# Revit family: FILTRATION FINALE SIMPLE-DUPLEX
name_source: partatom
category: Equipement de génie climatique
revit_build: Autodesk Revit 2018 (Build: 20170223_1515(x64)
units: mm (PartAtom-declared; Revit-internal decimal feet)

## family parameters
Basée sur le plan de construction = Non
Classification = Aucun
Cote de connecteur circulaire = Utiliser le diamètre
Couper avec des vides une fois chargée = Non
Partagée = Non
Point de calcul de pièce = Non
Toujours verticalement = Oui
Type d'élément = Normal

## types (10) — shared parameters

## per-type parameters (varying)
- FP 036 S: DESCR_ASPI=Entrée filtration; max.36m3/h; G1/2"FEM; DESCR_REFOUL=Sortie filtration; max.36m3/h; G1/2"FEM; DIAM_ASPI_AIR=15 mm  [stored 0.0492126 ft]; DIAM_REFOUL_AIR=15 mm  [stored 0.0492126 ft]; DUPLEX=Non; Debit_aspiration_air=36.0 m³/h; Debit_refoulement_air=36.0 m³/h; HAUTEUR=304 mm; HAUT_VANNE_VERTICALE=42.5 mm; LARGEUR=92 mm  [stored 0.301837 ft]; LARG_FIX=91.6 mm; LONGUEUR=449 mm; OFFEST_FILTRE=100 mm  [stored 0.328084 ft]; OFFEST_TUY1=25 mm  [stored 0.082021 ft]; OFFSET_CLAPET=228 mm; OFFSET_HAUT_TUY=425 mm; OFFSET_TUY2=416 mm; OFFSET_VANNE=25 mm  [stored 0.082021 ft]; OFFSET_VANNE2=345 mm; OFFSET_VANNE_VERTICALE=182 mm; POIDS(Kg)=2.5 mm  [stored 0.0082021 ft]; TAILLE_FILTRE=Filtre_Air_réduit : PAR 036; TAILLE_VANNE=Vanne papillon BS FF : DN15 - G1/2" - FF (231 0002)
- FP 072 S: DESCR_ASPI=Entrée filtration; max.72m3/h; G1/2"FEM; DESCR_REFOUL=Sortie filtration; max.72m3/h; G1/2"FEM; DIAM_ASPI_AIR=15 mm  [stored 0.0492126 ft]; DIAM_REFOUL_AIR=15 mm  [stored 0.0492126 ft]; DUPLEX=Non; Debit_aspiration_air=72.0 m³/h; Debit_refoulement_air=72.0 m³/h; HAUTEUR=352 mm; HAUT_VANNE_VERTICALE=71 mm  [stored 0.23294 ft]; LARGEUR=106 mm  [stored 0.347769 ft]; LARG_FIX=129 mm  [stored 0.423228 ft]; LONGUEUR=471 mm; OFFEST_FILTRE=111 mm; OFFEST_TUY1=99.9 mm; OFFSET_CLAPET=250 mm; OFFSET_HAUT_TUY=425 mm; OFFSET_TUY2=438 mm; OFFSET_VANNE=25 mm  [stored 0.082021 ft]; OFFSET_VANNE2=367 mm; OFFSET_VANNE_VERTICALE=205 mm; POIDS(Kg)=3 mm  [stored 0.00984252 ft]; TAILLE_FILTRE=Filtre_Air_réduit : PAR 072; TAILLE_VANNE=Vanne papillon BS FF : DN15 - G1/2" - FF (231 0002)
- FP 109 S: DESCR_ASPI=Entrée filtration; max.109m3/h; G3/4"FEM; DESCR_REFOUL=Sortie filtration; max.109m3/h; G3/4"FEM; DIAM_ASPI_AIR=20 mm  [stored 0.0656168 ft]; DIAM_REFOUL_AIR=20 mm  [stored 0.0656168 ft]; DUPLEX=Non; Debit_aspiration_air=109.0 m³/h; Debit_refoulement_air=109.0 m³/h; HAUTEUR=361 mm; HAUT_VANNE_VERTICALE=83 mm  [stored 0.27231 ft]; LARGEUR=106 mm  [stored 0.347769 ft]; LARG_FIX=129 mm  [stored 0.423228 ft]; LONGUEUR=508 mm; OFFEST_FILTRE=120 mm  [stored 0.393701 ft]; OFFEST_TUY1=99.9 mm; OFFSET_CLAPET=270 mm; OFFSET_HAUT_TUY=425 mm; OFFSET_TUY2=472 mm; OFFSET_VANNE=27 mm  [stored 0.0885827 ft]; OFFSET_VANNE2=391 mm; OFFSET_VANNE_VERTICALE=220 mm; POIDS(Kg)=4 mm  [stored 0.0131234 ft]; TAILLE_FILTRE=Filtre_Air_réduit : PAR 109; TAILLE_VANNE=Vanne papillon BS FF : DN20 - G3/4" - FF (231 0008)
- FP 396 S: DESCR_ASPI=Entrée filtration; max.396m3/h; G1"FEM; DESCR_REFOUL=Sortie filtration; max.396m3/h; G1"FEM; DIAM_ASPI_AIR=25 mm  [stored 0.082021 ft]; DIAM_REFOUL_AIR=25 mm  [stored 0.082021 ft]; DUPLEX=Non; Debit_aspiration_air=396.0 m³/h; Debit_refoulement_air=396.0 m³/h; HAUTEUR=496 mm; HAUT_VANNE_VERTICALE=93.5 mm  [stored 0.306759 ft]; LARGEUR=131 mm  [stored 0.42979 ft]; LARG_FIX=161 mm; LONGUEUR=620 mm; OFFEST_FILTRE=155 mm  [stored 0.50853 ft]; OFFEST_TUY1=99.9 mm; OFFSET_CLAPET=341 mm; OFFSET_HAUT_TUY=425 mm; OFFSET_TUY2=575 mm; OFFSET_VANNE=34.5 mm  [stored 0.113189 ft]; OFFSET_VANNE2=482 mm; OFFSET_VANNE_VERTICALE=284 mm; POIDS(Kg)=6.5 mm  [stored 0.0213255 ft]; TAILLE_FILTRE=Filtre_Air_réduit : PAR 396; TAILLE_VANNE=Vanne papillon BS FF : DN25 - G1" - FF (231 0001)
- FP 072 DP: DESCR_ASPI=Entrée filtration; max.72m3/h; G1/2"FEM; DESCR_REFOUL=Sortie filtration; max.72m3/h; G1/2"FEM; DIAM_ASPI_AIR=15 mm  [stored 0.0492126 ft]; DIAM_REFOUL_AIR=15 mm  [stored 0.0492126 ft]; DUPLEX=Oui; Debit_aspiration_air=72.0 m³/h; Debit_refoulement_air=72.0 m³/h; HAUTEUR=610 mm; HAUT_VANNE_VERTICALE=71 mm  [stored 0.23294 ft]; LARGEUR=92 mm  [stored 0.301837 ft]; LARG_FIX=108 mm  [stored 0.354331 ft]; LONGUEUR=529 mm; OFFEST_FILTRE=177 mm; OFFEST_TUY1=34 mm; OFFSET_CLAPET=306 mm; OFFSET_HAUT_TUY=306 mm; OFFSET_TUY2=494 mm; OFFSET_VANNE=104 mm; OFFSET_VANNE2=423 mm; OFFSET_VANNE_VERTICALE=260 mm; POIDS(Kg)=5.5 mm  [stored 0.0180446 ft]; TAILLE_FILTRE=Filtre_Air_réduit : PAR 036; TAILLE_VANNE=Vanne papillon BS FF : DN15 - G1/2" - FF (231 0002)
- FP 217 S: DESCR_ASPI=Entrée filtration; max.217m3/h; G3/4"FEM; DESCR_REFOUL=Sortie filtration; max.217m3/h; G3/4"FEM; DIAM_ASPI_AIR=20 mm  [stored 0.0656168 ft]; DIAM_REFOUL_AIR=20 mm  [stored 0.0656168 ft]; DUPLEX=Non; Debit_aspiration_air=217.0 m³/h; Debit_refoulement_air=217.0 m³/h; HAUTEUR=388 mm; HAUT_VANNE_VERTICALE=83 mm  [stored 0.27231 ft]; LARGEUR=131 mm  [stored 0.42979 ft]; LARG_FIX=161 mm; LONGUEUR=541 mm; OFFEST_FILTRE=137 mm  [stored 0.449475 ft]; OFFEST_TUY1=99.9 mm; OFFSET_CLAPET=303 mm; OFFSET_HAUT_TUY=425 mm; OFFSET_TUY2=504 mm; OFFSET_VANNE=27 mm  [stored 0.0885827 ft]; OFFSET_VANNE2=423 mm; OFFSET_VANNE_VERTICALE=252 mm; POIDS(Kg)=5.5 mm  [stored 0.0180446 ft]; TAILLE_FILTRE=Filtre_Air_réduit : PAR 217; TAILLE_VANNE=Vanne papillon BS FF : DN20 - G3/4" - FF (231 0008)
- FP 144 DP: DESCR_ASPI=Entrée filtration; max.144m3/h; G3/4"FEM; DESCR_REFOUL=Sortie filtration; max.144m3/h; G3/4"FEM; DIAM_ASPI_AIR=20 mm  [stored 0.0656168 ft]; DIAM_REFOUL_AIR=20 mm  [stored 0.0656168 ft]; DUPLEX=Oui; Debit_aspiration_air=144.0 m³/h; Debit_refoulement_air=144.0 m³/h; HAUTEUR=704 mm; HAUT_VANNE_VERTICALE=72 mm  [stored 0.23622 ft]; LARGEUR=106 mm  [stored 0.347769 ft]; LARG_FIX=130 mm  [stored 0.426509 ft]; LONGUEUR=558 mm; OFFEST_FILTRE=197 mm; OFFEST_TUY1=36 mm  [stored 0.11811 ft]; OFFSET_CLAPET=336 mm; OFFSET_HAUT_TUY=368 mm; OFFSET_TUY2=521 mm; OFFSET_VANNE=111 mm; OFFSET_VANNE2=453 mm; OFFSET_VANNE_VERTICALE=291 mm; POIDS(Kg)=6.5 mm  [stored 0.0213255 ft]; TAILLE_FILTRE=Filtre_Air_réduit : PAR 072; TAILLE_VANNE=Vanne papillon BS FF : DN20 - G3/4" - FF (231 0008)
- FP 218 DP: DESCR_ASPI=Entrée filtration; max.218m3/h; G3/4"FEM; DESCR_REFOUL=Sortie filtration; max.218m3/h; G3/4"FEM; DIAM_ASPI_AIR=20 mm  [stored 0.0656168 ft]; DIAM_REFOUL_AIR=20 mm  [stored 0.0656168 ft]; DUPLEX=Oui; Debit_aspiration_air=218.0 m³/h; Debit_refoulement_air=218.0 m³/h; HAUTEUR=711 mm; HAUT_VANNE_VERTICALE=83 mm  [stored 0.27231 ft]; LARGEUR=106 mm  [stored 0.347769 ft]; LARG_FIX=130 mm  [stored 0.426509 ft]; LONGUEUR=630 mm; OFFEST_FILTRE=225 mm; OFFEST_TUY1=45 mm  [stored 0.147638 ft]; OFFSET_CLAPET=375 mm; OFFSET_HAUT_TUY=413 mm; OFFSET_TUY2=585 mm; OFFSET_VANNE=131 mm  [stored 0.42979 ft]; OFFSET_VANNE2=495 mm; OFFSET_VANNE_VERTICALE=324 mm; POIDS(Kg)=8 mm  [stored 0.0262467 ft]; TAILLE_FILTRE=Filtre_Air_réduit : PAR 109; TAILLE_VANNE=Vanne papillon BS FF : DN20 - G3/4" - FF (231 0008)
- FP 434 DP: DESCR_ASPI=Entrée filtration; max.434m3/h; G1"FEM; DESCR_REFOUL=Sortie filtration; max.434m3/h; G1"FEM; DIAM_ASPI_AIR=25 mm  [stored 0.082021 ft]; DIAM_REFOUL_AIR=25 mm  [stored 0.082021 ft]; DUPLEX=Oui; Debit_aspiration_air=434.0 m³/h; Debit_refoulement_air=434.0 m³/h; HAUTEUR=809 mm; HAUT_VANNE_VERTICALE=83 mm  [stored 0.27231 ft]; LARGEUR=131 mm  [stored 0.42979 ft]; LARG_FIX=161 mm; LONGUEUR=663 mm; OFFEST_FILTRE=241 mm; OFFEST_TUY1=45 mm  [stored 0.147638 ft]; OFFSET_CLAPET=407 mm; OFFSET_HAUT_TUY=445 mm; OFFSET_TUY2=618 mm; OFFSET_VANNE=132 mm  [stored 0.433071 ft]; OFFSET_VANNE2=528 mm; OFFSET_VANNE_VERTICALE=357 mm; POIDS(Kg)=12 mm  [stored 0.0393701 ft]; TAILLE_FILTRE=Filtre_Air_réduit : PAR 217; TAILLE_VANNE=Vanne papillon BS FF : DN25 - G1" - FF (231 0001)
- FP 792 DP: DESCR_ASPI=Entrée filtration; max.792m3/h; G1"1/4FEM; DESCR_REFOUL=Sortie filtration; max.792m3/h; G1"1/4FEM; DIAM_ASPI_AIR=32 mm  [stored 0.104987 ft]; DIAM_REFOUL_AIR=32 mm  [stored 0.104987 ft]; DUPLEX=Oui; Debit_aspiration_air=792.0 m³/h; Debit_refoulement_air=792.0 m³/h; Fabricant=MIL'S; HAUTEUR=929 mm; HAUT_VANNE_VERTICALE=97 mm  [stored 0.318241 ft]; LARGEUR=142 mm  [stored 0.465879 ft]; LARG_FIX=161 mm; LONGUEUR=965 mm; Lien espace client=https://www.mils.fr; Modèle=Filtration finale FP; OFFEST_FILTRE=263 mm; OFFEST_TUY1=45 mm  [stored 0.147638 ft]; OFFSET_CLAPET=684 mm; OFFSET_HAUT_TUY=492 mm; OFFSET_TUY2=922 mm; OFFSET_VANNE=144 mm  [stored 0.472441 ft]; OFFSET_VANNE2=826 mm; OFFSET_VANNE_VERTICALE=627 mm; POIDS(Kg)=14 mm  [stored 0.0459318 ft]; TAILLE_FILTRE=Filtre_Air_réduit : PAR 396; TAILLE_VANNE=Vanne papillon BS FF : DN32 - G1"1/4 - FF (231 0005)

note: [stored X ft] marks values corroborated as IEEE doubles in the binary element streams (Revit-internal decimal feet)

## geometry (parser evidence)
native form markers: Sweep x9
no freeform markers — native parametric forms only
